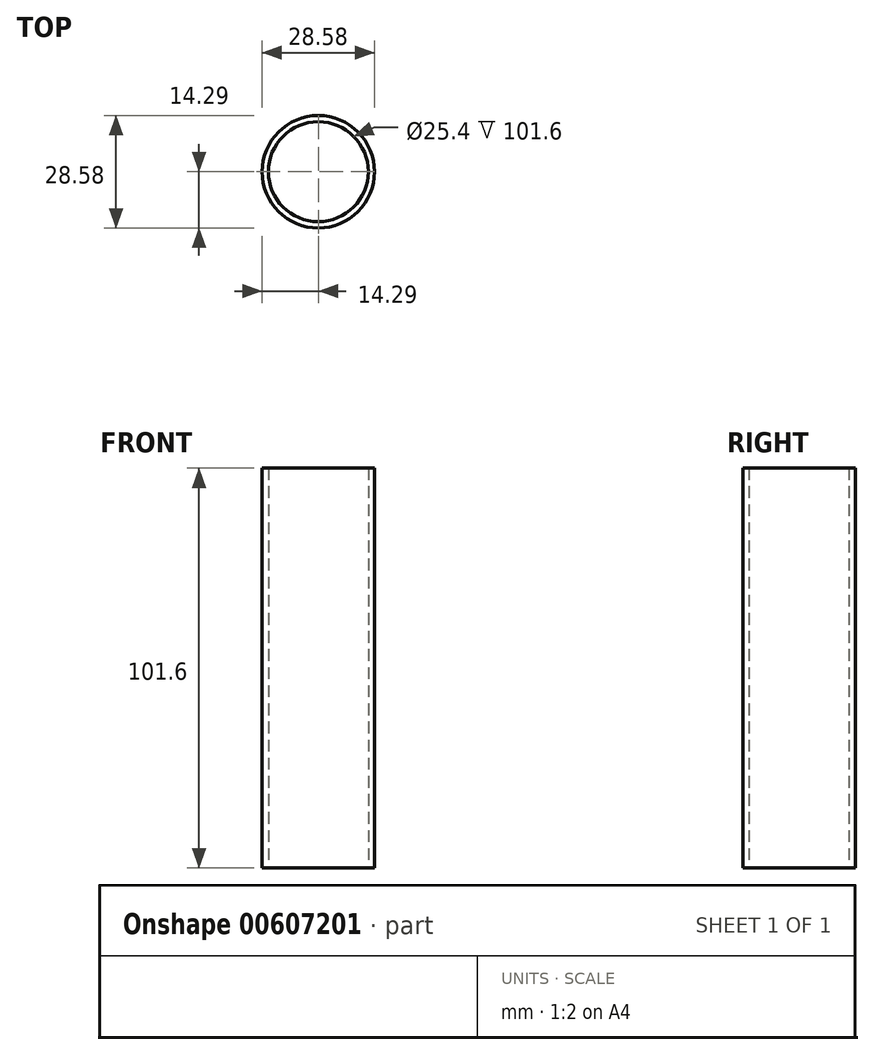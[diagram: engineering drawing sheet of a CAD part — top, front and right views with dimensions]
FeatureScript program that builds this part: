
annotation { "Feature Type Name" : "Feature", "Feature Type Description" : "" }
export const myFeature = defineFeature(function(context is Context, id is Id, definition is map)
    precondition{}
    {
        {
            var Q0;
            Q0=qCreatedBy(makeId("Top.planeOp"),FACE);
            var sketch = newSketch(context, id + "F0", { "sketchPlane" : qUnion([Q0])});
            skLineSegment(sketch, "E0", {"start": v(0, 0) * mm, "end": v(12.7, 0) * mm});
            skCircle(sketch, "E1", {"center": v(0, 0) * mm, "radius": 12.7 * mm});
            skCircle(sketch, "E2.0", {"center": v(0, 0) * mm, "radius": 14.29 * mm});
            skSolve(sketch);
        }
        {
            var Q0;
            Q0=qCreatedBy(makeId("Top.planeOp"),FACE);
            var sketch = newSketch(context, id + "F1", { "sketchPlane" : qUnion([Q0])});
            skSolve(sketch);
        }
        {
            var Q0;
            Q0=qSketchRegion(id+"F1",true);
            var Q1;
            Q1=makeQuery(id+"F0.imprint","IMPRINT",FACE,{"disambiguationData":[TD([[makeQuery(id+"F0.imprint","IMPRINT",EDGE,{"derivedFrom":sQuery(id+"F0.wireOp",EDGE,"E1")}),-1.0]])]});
            extrude(context, id + "F2", {"entities" : qUnion([Q0, Q1]), "depth" : 101.6 * mm, "offsetDistance" : 25.4 * mm});
        }
    });
